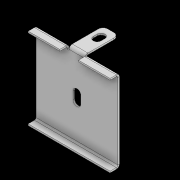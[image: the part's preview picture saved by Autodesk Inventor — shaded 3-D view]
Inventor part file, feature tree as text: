
AUTODESK INVENTOR PART (.ipt)
format: ipt  version: 2021 (Build 250183000, 183)  size: 179,200 bytes
history: native  units: mm
features: sheet_metal_op x5, sketch x5, other x4, chamfer x1
ambient origin geometry x8: Origin, YZ Plane, XZ Plane, XY Plane, X Axis, Y Axis, Z Axis, Center Point
bodies: Solid1 (feature_tree)
feature tree (15):
  sheet_metal_op  "Face1"
  sheet_metal_op  "Flange1"
  sheet_metal_op  "Fold1"
  chamfer  "Corner Round1"
  sketch  "Sketch1"  dims[d0=105.0mm]
  other  "Plate1"
  sketch  "Sketch2"  dims[d1=145.0mm]
  sketch  "Sketch3"  dims[d2=2.0mm]
  other  "Plate2"
  sheet_metal_op  "Bend1"
  sheet_metal_op  "Corner1"
  sketch  "Sketch4"  dims[d3=20.0mm]
  sketch  "Sketch5"  dims[d4=105.0mm d5=2.0mm d6=0.0mm d7=2.0mm d8=1.0mm d9=4.0mm d10=2.0mm d11=10.0mm d12=90.0deg d13=2.0mm d14=8.0mm d15=2.0mm d16=2.0mm d17=2.0mm d18=1.0mm d19=4.0mm d20=2.0mm d21=90.0deg d22=2.0mm d23=10.0mm d24=52.5mm d25=5.0mm d26=5.0mm d27=5.0mm d28=15.0mm d29=2.0mm d30=0.0mm d31=6.0mm]
  other  "Cut1"
  other  "Cut2"
